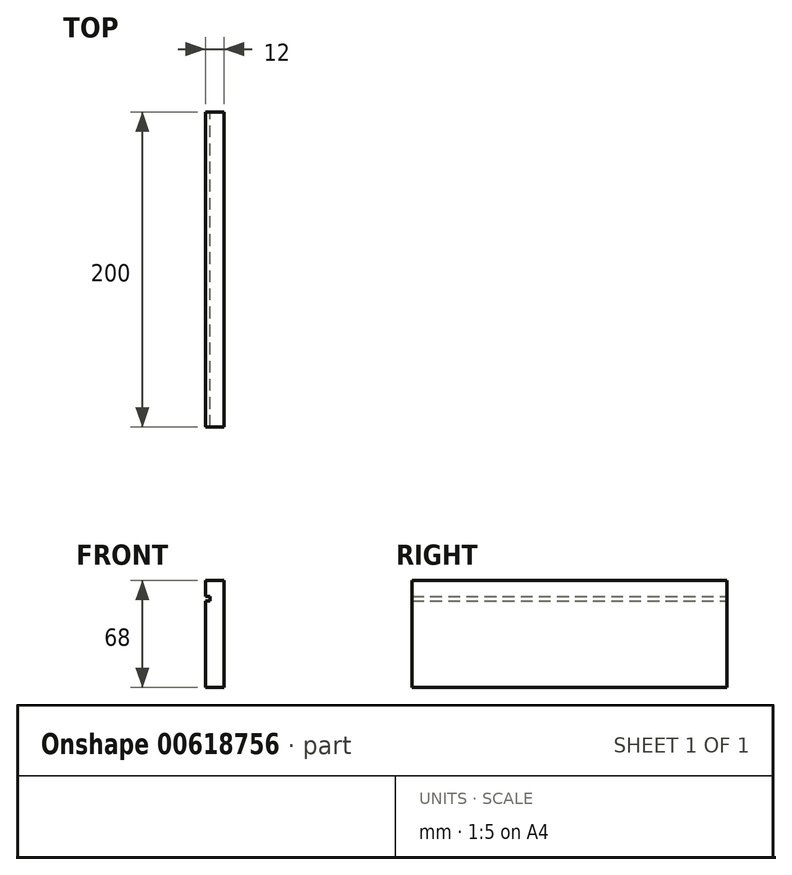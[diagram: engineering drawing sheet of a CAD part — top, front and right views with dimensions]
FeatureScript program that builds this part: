
annotation { "Feature Type Name" : "Feature", "Feature Type Description" : "" }
export const myFeature = defineFeature(function(context is Context, id is Id, definition is map)
    precondition{}
    {
        {
            var Q0;
            Q0=qCreatedBy(makeId("Front.planeOp"),FACE);
            var sketch = newSketch(context, id + "F0", { "sketchPlane" : qUnion([Q0])});
            skLineSegment(sketch, "E0.bottom", {"start": v(6, -34) * mm, "end": v(-6, -34) * mm});
            skLineSegment(sketch, "E0.top", {"start": v(6, 34) * mm, "end": v(-6, 34) * mm});
            skLineSegment(sketch, "E0.left", {"start": v(6, -34) * mm, "end": v(6, 34) * mm});
            skLineSegment(sketch, "E0.right", {"start": v(-6, -34) * mm, "end": v(-6, 21) * mm});
            skPoint(sketch, "E0.middle", {"position": v(0, 0) * mm});
            skLineSegment(sketch, "E1", {"start": v(-6, 34) * mm, "end": v(-6, 24) * mm});
            skLineSegment(sketch, "E2", {"start": v(-6, 24) * mm, "end": v(-3, 24) * mm});
            skLineSegment(sketch, "E3", {"start": v(-3, 24) * mm, "end": v(-3, 21) * mm});
            skLineSegment(sketch, "E4", {"start": v(-3, 21) * mm, "end": v(-6, 21) * mm});
            skLineSegment(sketch, "E5.trimOffspring", {"start": v(-6, 24) * mm, "end": v(-6, 34) * mm});
            skSolve(sketch);
        }
        {
            var Q0;
            Q0=makeQuery(id+"F0.imprint","IMPRINT",FACE,{"disambiguationData":[TD([[makeQuery(id+"F0.imprint","IMPRINT",EDGE,{"derivedFrom":sQuery(id+"F0.wireOp",EDGE,"E0.bottom")}),-1.0]])]});
            extrude(context, id + "F1", {"entities" : qUnion([Q0]), "depth" : 200 * mm, "offsetDistance" : 25 * mm});
        }
    });
